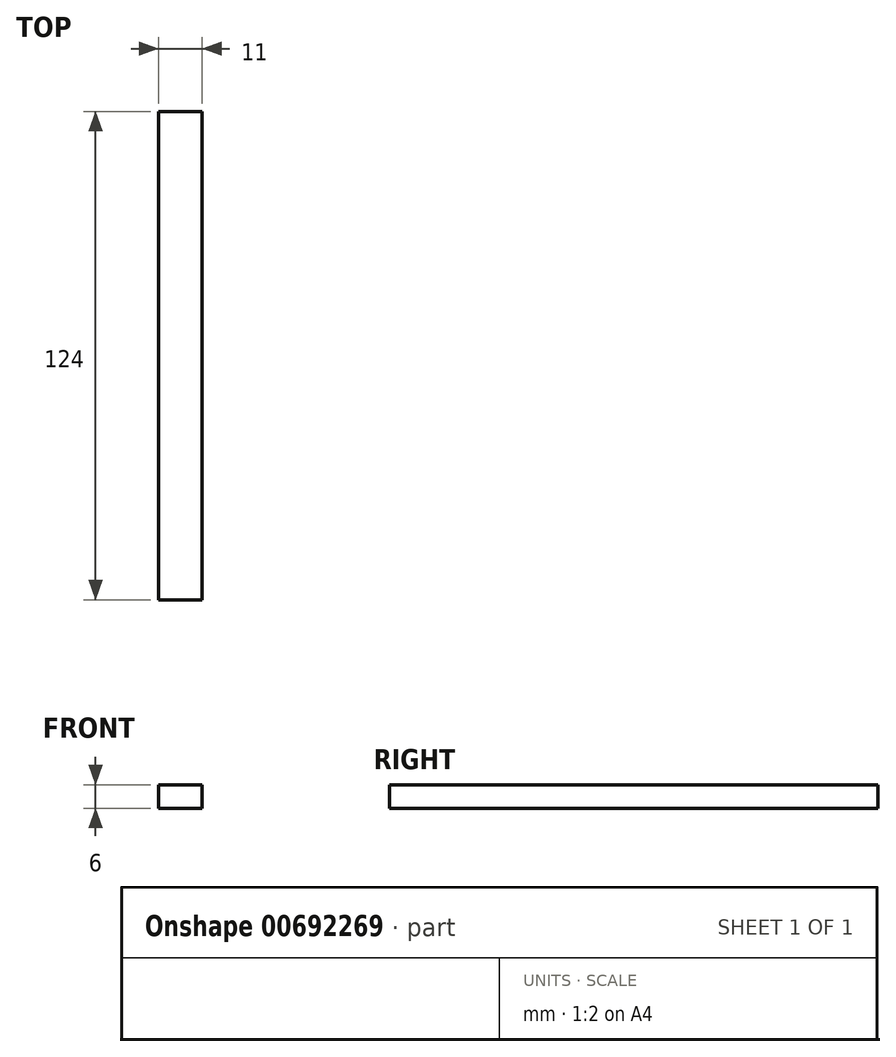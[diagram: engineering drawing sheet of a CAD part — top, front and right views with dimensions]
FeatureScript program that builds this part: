
annotation { "Feature Type Name" : "Feature", "Feature Type Description" : "" }
export const myFeature = defineFeature(function(context is Context, id is Id, definition is map)
    precondition{}
    {
        {
            var Q0;
            Q0=qCreatedBy(makeId("Top.planeOp"),FACE);
            var sketch = newSketch(context, id + "F0", { "sketchPlane" : qUnion([Q0])});
            skLineSegment(sketch, "E0.bottom", {"start": v(0, 0) * mm, "end": v(11, 0) * mm});
            skLineSegment(sketch, "E0.top", {"start": v(0, 124) * mm, "end": v(11, 124) * mm});
            skLineSegment(sketch, "E0.left", {"start": v(0, 0) * mm, "end": v(0, 124) * mm});
            skLineSegment(sketch, "E0.right", {"start": v(11, 0) * mm, "end": v(11, 124) * mm});
            skSolve(sketch);
        }
        {
            var Q0;
            Q0 = qSketchRegion(id + "F0", true);
            extrude(context, id + "F1", {"entities" : qUnion([Q0]), "depth" : 6 * mm, "offsetDistance" : 25.4 * mm});
        }
    });
